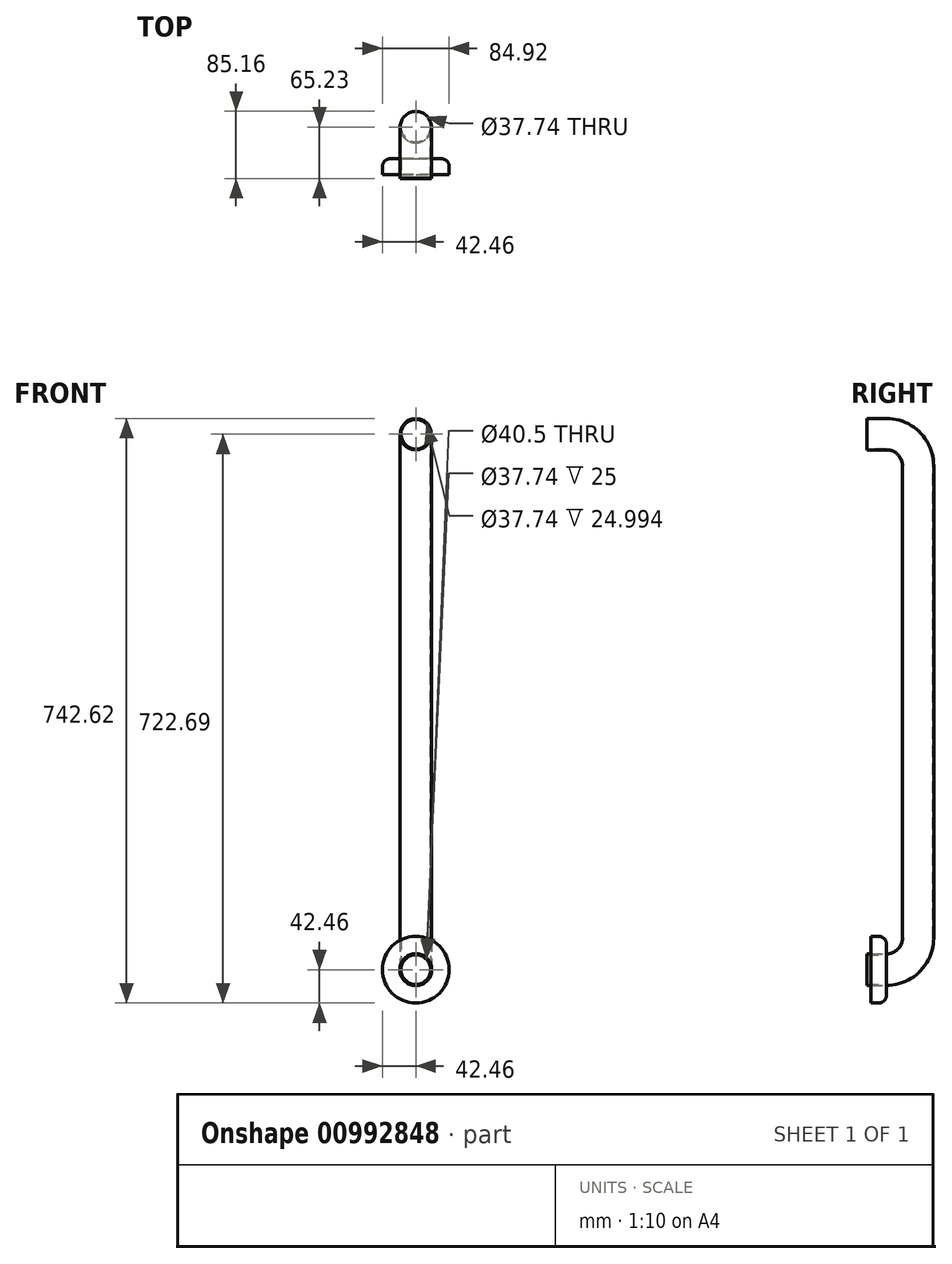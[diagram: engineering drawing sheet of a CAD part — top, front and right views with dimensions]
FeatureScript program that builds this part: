
annotation { "Feature Type Name" : "Feature", "Feature Type Description" : "" }
export const myFeature = defineFeature(function(context is Context, id is Id, definition is map)
    precondition{}
    {
        {
            var Q0;
            Q0=qCreatedBy(makeId("Front.planeOp"),FACE);
            var sketch = newSketch(context, id + "F0", { "sketchPlane" : qUnion([Q0])});
            skCircle(sketch, "E0", {"center": v(0, 0) * mm, "radius": 19.93 * mm});
            skCircle(sketch, "E1", {"center": v(0, 0) * mm, "radius": 18.87 * mm});
            skSolve(sketch);
        }
        {
            var Q0;
            Q0=qCreatedBy(makeId("Right.planeOp"),FACE);
            var sketch = newSketch(context, id + "F1", { "sketchPlane" : qUnion([Q0])});
            skArc(sketch, "E2", {"start": v(0, 0) * mm, "mid": v(28.45, 11.78) * mm, "end": v(40.23, 40.23) * mm});
            skLineSegment(sketch, "E3", {"start": v(0, 40.23) * mm, "end": v(0, 0) * mm});
            skLineSegment(sketch, "E4", {"start": v(0, 40.23) * mm, "end": v(40.23, 40.23) * mm});
            skLineSegment(sketch, "E5", {"start": v(40.23, 40.23) * mm, "end": v(40.23, 640.23) * mm});
            skArc(sketch, "E6", {"start": v(40.23, 640.23) * mm, "mid": v(28.51, 668.51) * mm, "end": v(0.23, 680.23) * mm});
            skLineSegment(sketch, "E7", {"start": v(40.23, 640.23) * mm, "end": v(0.23, 640.23) * mm});
            skLineSegment(sketch, "E8", {"start": v(0.23, 640.23) * mm, "end": v(0.23, 680.23) * mm});
            skLineSegment(sketch, "E9", {"start": v(0.23, 680.23) * mm, "end": v(-24.76, 680.23) * mm});
            skSolve(sketch);
        }
        {
            var Q0;
            Q0=makeQuery(id+"F0.imprint","IMPRINT",FACE,{"disambiguationData":[TD([[makeQuery(id+"F0.imprint","IMPRINT",EDGE,{"derivedFrom":sQuery(id+"F0.wireOp",EDGE,"E0")}),1.0]])]});
            extrude(context, id + "F2", {"entities" : qUnion([Q0]), "depth" : 25 * mm, "offsetDistance" : 25 * mm});
        }
        {
            var Q0;
            Q0=makeQuery(id+"F2.opExtrude","CAP_FACE",FACE,{"disambiguationData":[OSD([sQuery(id+"F0.wireOp",EDGE,"E0"),sQuery(id+"F0.wireOp",EDGE,"E1")])],"isStart":true});
            var Q1;
            Q1=sQuery(id+"F1.wireOp",EDGE,"E2");
            var Q2;
            Q2=sQuery(id+"F1.wireOp",EDGE,"E5");
            var Q3;
            Q3=sQuery(id+"F1.wireOp",EDGE,"E6");
            var Q4;
            Q4=sQuery(id+"F1.wireOp",EDGE,"E9");
            sweep(context, id + "F3", {"profiles" : qUnion([Q0]), "path" : qUnion([Q1, Q2, Q3, Q4])});
        }
        {
            var Q0;
            Q0=qCreatedBy(makeId("Front.planeOp"),FACE);
            var sketch = newSketch(context, id + "F4", { "sketchPlane" : qUnion([Q0])});
            skCircle(sketch, "E10", {"center": v(0, 0) * mm, "radius": 20.25 * mm});
            skCircle(sketch, "E11", {"center": v(0, 0) * mm, "radius": 42.46 * mm});
            skSolve(sketch);
        }
        {
            var Q0;
            Q0=makeQuery(id+"F4.imprint","IMPRINT",FACE,{"disambiguationData":[TD([[makeQuery(id+"F4.imprint","IMPRINT",EDGE,{"derivedFrom":sQuery(id+"F4.wireOp",EDGE,"E10")}),-1.0]])]});
            extrude(context, id + "F5", {"entities" : qUnion([Q0]), "depth" : 20 * mm, "offsetDistance" : 25 * mm});
        }
        {
            var Q0;
            Q0=makeQuery(id+"F5.opExtrude","CAP_EDGE",EDGE,{"disambiguationData":[OSD([sQuery(id+"F4.wireOp",EDGE,"E11")])],"isStart":true});
            fillet(context, id + "F6", {"entities" : qUnion([Q0]), "tangentPropagation" : true, "radius" : 10 * mm, "defaultsChanged" : true, "vertexSettings" : [], "allowEdgeOverflow" : false});
        }
    });
